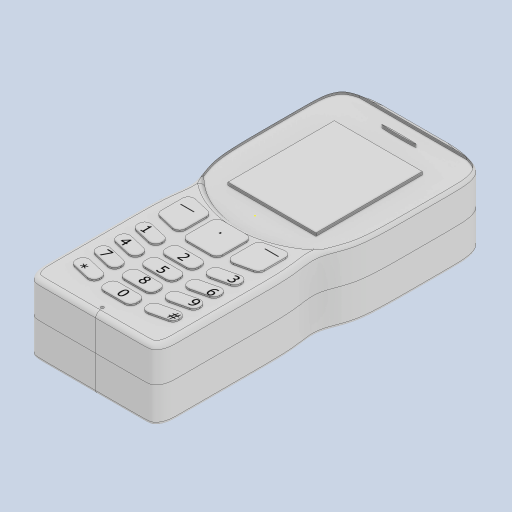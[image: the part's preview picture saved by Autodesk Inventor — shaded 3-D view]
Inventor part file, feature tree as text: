
AUTODESK INVENTOR PART (.ipt)
format: ipt  version: 2024 (Build 280153020, 153B)  size: 657,408 bytes
history: native  units: mm
features: sketch x11, extrude x9, fillet x6, projected_geometry x4, other x2, mirror x2, pattern_linear x2, hole x1
ambient origin geometry x8: Origin, YZ Plane, XZ Plane, XY Plane, X Axis, Y Axis, Z Axis, Center Point
bodies: Body1 (feature_tree), Body2 (feature_tree)
feature tree (37):
  other  "Bottom"
  extrude  "Extrusion1"  Depth=12.0mm TaperAngle=0.0deg
  extrude  "Extrusion2"  Depth=12.0mm
  extrude  "Extrusion3"  Depth=15.0mm
  sketch  "Sketch4"  dims[d14=5.8mm d15=5.0mm]
  extrude  "Extrusion4"  Depth=5.0mm
  extrude  "Extrusion5"  Depth=1.0mm TaperAngle=0.0deg
  extrude  "Extrusion6"  Depth=12.0mm
  extrude  "Extrusion7"  Depth=13.0mm
  mirror  "Mirror1"
  fillet  "Fillet2"  Radius=0.5mm
  extrude  "Extrusion8"  Depth=9.5mm
  fillet  "Fillet3"  Radius=8.010086mm
  pattern_linear  "Rectangular Pattern2"  Spacing1=5.0mm  [1 undecoded]
  extrude  "Extrusion9"  Depth=24.394704mm
  fillet  "Fillet4"  Radius=28.352226mm
  pattern_linear  "Rectangular Pattern3"  Spacing1=0.5mm  [1 undecoded]
  mirror  "Mirror2"
  hole  "Hole1"  [1 undecoded]
  sketch  "Sketch12"  dims[d39=11.0mm d40=5.0mm d41=24.394704mm d42=28.352226mm d43=0.5mm d44=0.0mm d45=2.0mm d46=40.0mm d48=7.0mm d49=9.501687mm d50=8.011776mm d51=0.059806mm d52=4.397577mm d53=0.5mm d54=0.0mm d55=2.0mm d56=40.0mm d58=7.0mm d59=1.0mm d60=6.0mm d61=4.0mm d62=2.0mm d63=90.0deg d64=20.0mm d65=20.594885mm d67=1.0mm d69=1.6mm d70=2.0mm]
  fillet  "Fillet6"  Radius=40.0mm
  fillet  "Fillet8"  Radius=9.501687mm
  fillet  "Fillet9"  Radius=8.011776mm
  sketch  "Sketch1"  dims[d4=12.0mm d5=0.0mm d6=12.0mm d7=0.0mm]
  sketch  "Sketch2"  dims[d8=1.0mm d9=0.0mm d10=12.0mm]
  projected_geometry  "Projected Loop1"
  other  "Top"
  sketch  "Sketch3"  dims[d12=15.0mm d13=15.0mm]
  sketch  "Sketch5"  dims[d16=5.870515mm d17=1.0mm d18=0.0mm]
  sketch  "Sketch6"  dims[d19=1.0mm d20=0.0mm d21=12.0mm]
  projected_geometry  "Projected Loop2"
  sketch  "Sketch8"  dims[d22=12.0mm d23=13.0mm d24=0.5mm d25=0.0mm]
  sketch  "Sketch9"  dims[d33=11.0mm d34=9.5mm d35=8.010086mm]
  projected_geometry  "Projected Loop3"
  sketch  "Sketch10"  dims[d36=0.5mm d37=0.0mm]
  projected_geometry  "Projected Loop4"
  sketch  "Sketch11"  dims[d38=2.0mm]
note: 3 required parameter values undecoded (feature->parameter linkage not recoverable at this tier; creation-order binding heuristic only, values carry confidence <= 0.55)
